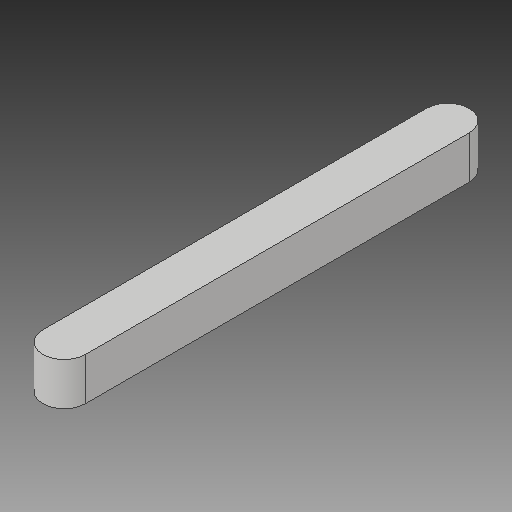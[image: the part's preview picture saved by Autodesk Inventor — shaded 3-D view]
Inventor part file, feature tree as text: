
AUTODESK INVENTOR PART (.ipt)
format: ipt  version: 2017 (Build 210142000, 142)  size: 78,848 bytes
history: native  units: in
note: dims shown in document units (in); Inventor stores cm internally (conversion verified against a paired STEP export)
features: fillet x1
ambient origin geometry x8: Origin, YZ Plane, XZ Plane, XY Plane, X Axis, Y Axis, Z Axis, Center Point
bodies: Solid1 (feature_tree)
feature tree (1):
  fillet  "Fillet1"  [1 undecoded]
note: 1 required parameter value undecoded (feature->parameter linkage not recoverable at this tier; creation-order binding heuristic only, values carry confidence <= 0.55)
